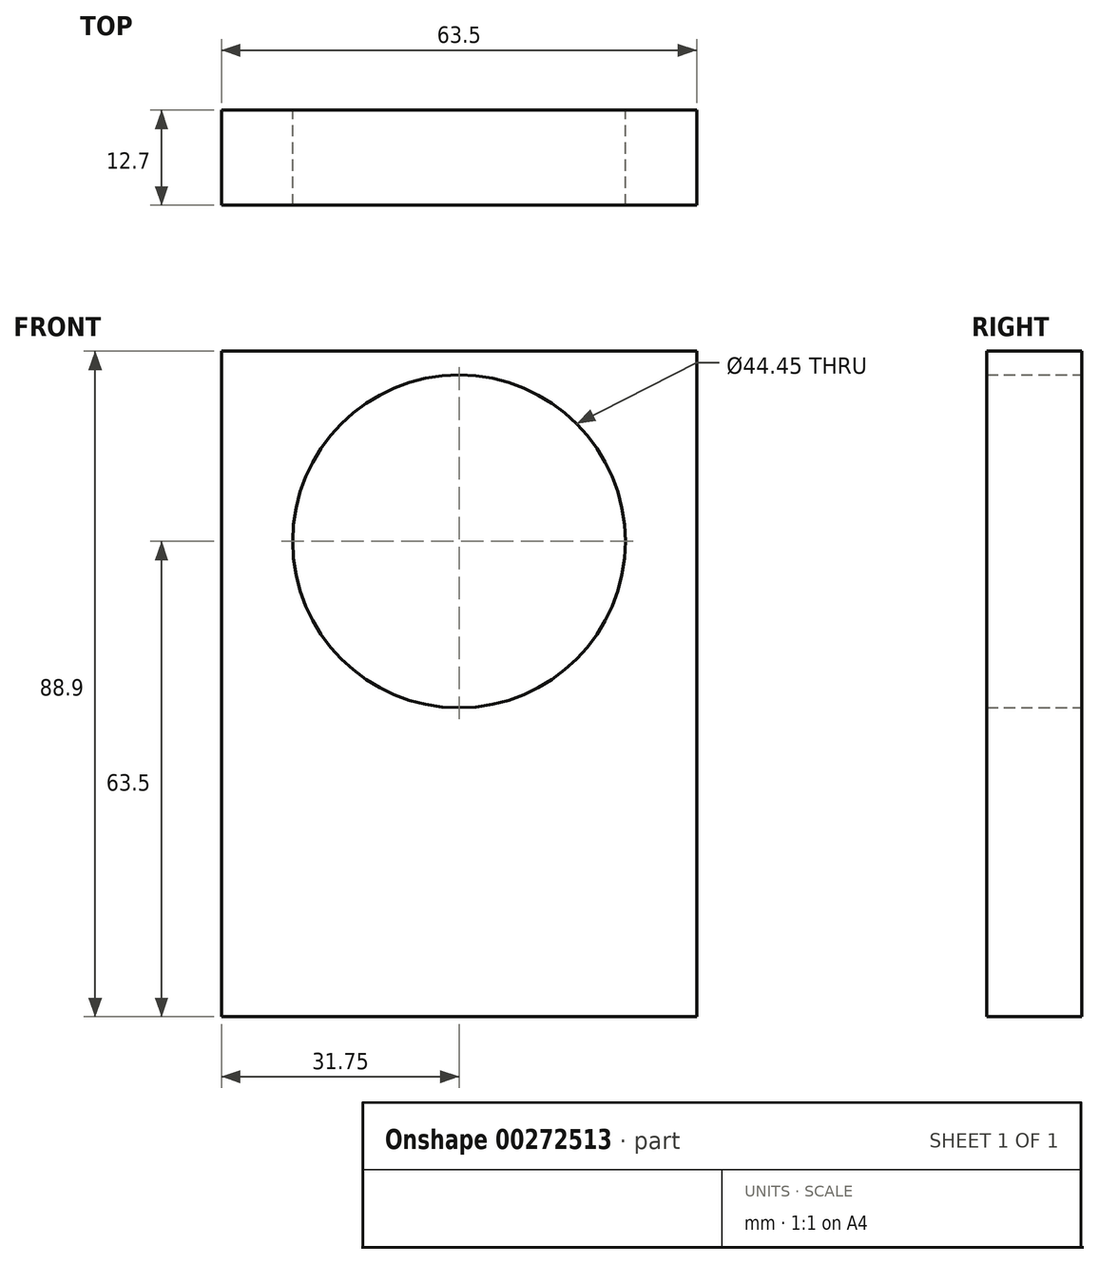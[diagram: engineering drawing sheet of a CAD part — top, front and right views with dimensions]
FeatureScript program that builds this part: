
annotation { "Feature Type Name" : "Feature", "Feature Type Description" : "" }
export const myFeature = defineFeature(function(context is Context, id is Id, definition is map)
    precondition{}
    {
        {
            var Q0;
            Q0=qCreatedBy(makeId("Front.planeOp"),FACE);
            var sketch = newSketch(context, id + "F0", { "sketchPlane" : qUnion([Q0])});
            skLineSegment(sketch, "E0.bottom", {"start": v(-31.75, 44.45) * mm, "end": v(31.75, 44.45) * mm});
            skLineSegment(sketch, "E0.top", {"start": v(-31.75, -44.45) * mm, "end": v(31.75, -44.45) * mm});
            skLineSegment(sketch, "E0.left", {"start": v(-31.75, 44.45) * mm, "end": v(-31.75, -44.45) * mm});
            skLineSegment(sketch, "E0.right", {"start": v(31.75, 44.45) * mm, "end": v(31.75, -44.45) * mm});
            skPoint(sketch, "E0.middle", {"position": v(0, 0) * mm});
            skLineSegment(sketch, "E1", {"start": v(0, 44.45) * mm, "end": v(0, 19.05) * mm});
            skPoint(sketch, "E1.endSnap0", {"position": v(0, 44.45) * mm});
            skCircle(sketch, "E2", {"center": v(0, 19.05) * mm, "radius": 22.23 * mm});
            skSolve(sketch);
        }
        {
            var Q0;
            Q0 = qSketchRegion(id + "F0", true);
            extrude(context, id + "F1", {"entities" : qUnion([Q0]), "depth" : 12.7 * mm});
        }
    });
